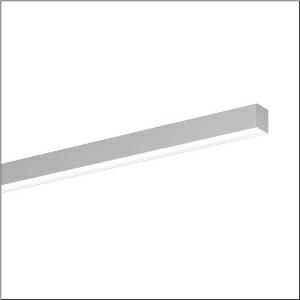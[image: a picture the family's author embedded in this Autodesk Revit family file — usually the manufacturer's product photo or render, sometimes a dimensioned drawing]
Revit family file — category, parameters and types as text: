
# Revit family: silica_r__21_51mx23da44sb_489f
name_source: partatom
category: Lighting Fixtures
units: mm (PartAtom-declared; Revit-internal decimal feet)

## family parameters
Cut with Voids When Loaded = No
Host = Face
Light Source = No
Part Type = Normal
Room Calculation Point = No
Round Connector Dimension = Use Diameter
Shared = No

## types (1)
- --- (1 x LED, 3280 lm, 22.4 W, 4000K)
    Apparent Load = 22 VA
    CIE Flux Codes = 78 96 99 100 100
    Color Rendering = 80
    Color Temperature = 4000K
    Default Elevation = 1800 mm
    Description = Silica® 21, office luminaire, primary optical cover: prismatic diffuser, of PMMA, CAT 2 (L<= 3000cd/m²), light emission: direct distribution, primary light characteristic: symmetric, installation type: surface-mounted, LED, rated luminous flux: 3.280lm, luminous efficacy: 146lm/W, light colour: 840, colour temperature: 4000K, control gear: DALI 2, with terminal, 3+2-pole, max. 2.5mm², mains connection: 220..240V, AC, 50/60Hz, rated input power: 22.4W, luminaire housing, of aluminium, metallic grey (RAL 9006), length: 1.204mm, width: 53mm, height: 53mm, protection rating (complete): IP20, insulation class (complete): insulation class I (protective earthing), certification: CE, permissible operating ambient temperature: 0..+35°C, standard: EN 50419, packaging unit: 1 piece
    Height = 53 mm
    Lamp = 1 x LED
    Lamp Light Flux = 3280 lm
    Lamp Power = 22.4 W
    Lamp count = 1
    Length = 1204 mm
    Luminous efficacy = 146 lm/W
    Manufacturer = Siteco
    ModVariant = No
    Model = 51MX23DA44SB
    Mounting Place = Ceiling
    Mounting Type = Surface mounted
    Number of Poles = 1
    OnlyDefault = Yes
    Power Factor = 1
    Product Name = Silica® 21
    Product group = office luminaire | ceiling mounted
    ProductGroupID = 302
    Protection Class = Protection class I
    Protection Degree = IP 20
    RLX_Detail_Level = 1
    RLX_Emergency_Light_Flux = 0 lm
    RLX_Emergency_Type = 0
    RLX_Emergency_Type_DB = No
    RlxData = <blob elided: 21149 chars, md5=6313f699>
    Socket = socket
    Standby Power = 0 W
    System Light Flux = 3280 lm
    System Power = 22 W
    Type Comments = factory setting: luminous flux: 100 % | dim-lin: 254 | 323 mA
    Type Image = l_1335933.jpg
    URL = http://relux.com
    VarID = @adj_007869
    Voltage = 0 V
    Weight = 0.00 kg
    Width = 53 mm

## geometry (parser evidence)
native form markers: Blend x4, Sweep x10
no freeform markers — native parametric forms only
